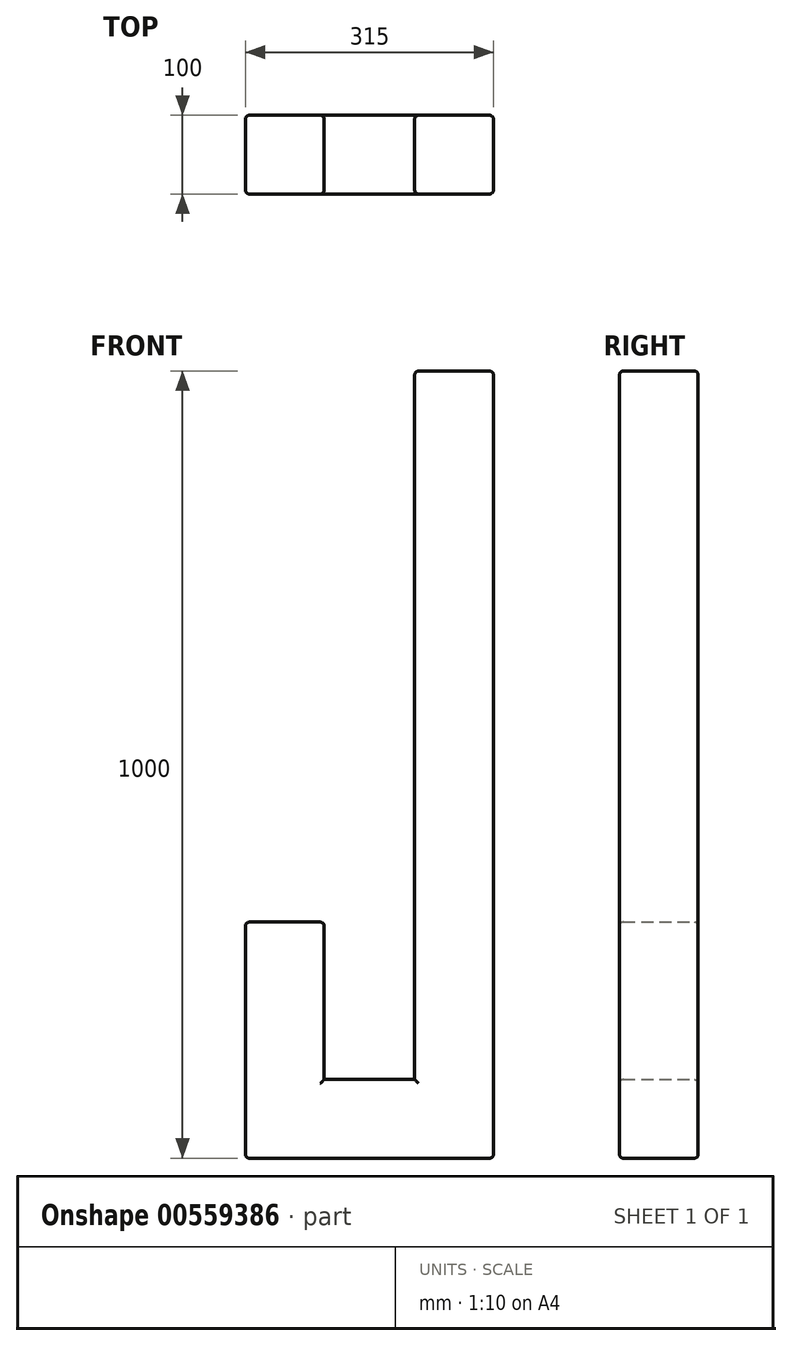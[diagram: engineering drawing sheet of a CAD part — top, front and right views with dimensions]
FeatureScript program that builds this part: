
annotation { "Feature Type Name" : "Feature", "Feature Type Description" : "" }
export const myFeature = defineFeature(function(context is Context, id is Id, definition is map)
    precondition{}
    {
        {
            var Q0;
            Q0=qCreatedBy(makeId("Front.planeOp"),FACE);
            var sketch = newSketch(context, id + "F0", { "sketchPlane" : qUnion([Q0])});
            skLineSegment(sketch, "E0", {"start": v(0, 0) * mm, "end": v(-100, 0) * mm});
            skLineSegment(sketch, "E1", {"start": v(-100, 0) * mm, "end": v(-100, -300) * mm});
            skLineSegment(sketch, "E2", {"start": v(-100, -300) * mm, "end": v(215, -300) * mm});
            skLineSegment(sketch, "E3", {"start": v(215, -300) * mm, "end": v(215, 700) * mm});
            skLineSegment(sketch, "E4", {"start": v(215, 700) * mm, "end": v(115, 700) * mm});
            skLineSegment(sketch, "E5", {"start": v(115, 700) * mm, "end": v(115, -200) * mm});
            skLineSegment(sketch, "E6", {"start": v(115, -200) * mm, "end": v(0, -200) * mm});
            skLineSegment(sketch, "E7", {"start": v(0, 0) * mm, "end": v(0, -200) * mm});
            skSolve(sketch);
        }
        {
            var Q0;
            Q0=makeQuery(id+"F0.imprint","IMPRINT",FACE,{"disambiguationData":[TD([[makeQuery(id+"F0.imprint","IMPRINT",EDGE,{"derivedFrom":sQuery(id+"F0.wireOp",EDGE,"E0")}),1.0]])]});
            extrude(context, id + "F1", {"entities" : qUnion([Q0]), "depth" : 100 * mm, "offsetDistance" : 25 * mm});
        }
        {
            var Q0;
            Q0=makeQuery(id+"F1.opExtrude","CAP_EDGE",EDGE,{"disambiguationData":[OSD([sQuery(id+"F0.wireOp",EDGE,"E1")])],"isStart":false});
            var Q1;
            Q1=makeQuery(id+"F1.opExtrude","CAP_EDGE",EDGE,{"disambiguationData":[OSD([sQuery(id+"F0.wireOp",EDGE,"E5")])],"isStart":false});
            var Q2;
            Q2=makeQuery(id+"F1.opExtrude","CAP_EDGE",EDGE,{"disambiguationData":[OSD([sQuery(id+"F0.wireOp",EDGE,"E6")])],"isStart":false});
            var Q3;
            Q3=makeQuery(id+"F1.opExtrude","CAP_EDGE",EDGE,{"disambiguationData":[OSD([sQuery(id+"F0.wireOp",EDGE,"E7")])],"isStart":false});
            var Q4;
            Q4=makeQuery(id+"F1.opExtrude","CAP_EDGE",EDGE,{"disambiguationData":[OSD([sQuery(id+"F0.wireOp",EDGE,"E0")])],"isStart":false});
            var Q5;
            Q5=makeQuery(id+"F1.opExtrude","SWEPT_EDGE",EDGE,{"disambiguationData":[OSD([sQuery(id+"F0.wireOp",EDGE,"E0"),sQuery(id+"F0.wireOp",EDGE,"E1")])]});
            var Q6;
            Q6=makeQuery(id+"F1.opExtrude","CAP_EDGE",EDGE,{"disambiguationData":[OSD([sQuery(id+"F0.wireOp",EDGE,"E1")])],"isStart":true});
            var Q7;
            Q7=makeQuery(id+"F1.opExtrude","SWEPT_EDGE",EDGE,{"disambiguationData":[OSD([sQuery(id+"F0.wireOp",EDGE,"E1"),sQuery(id+"F0.wireOp",EDGE,"E2")])]});
            var Q8;
            Q8=makeQuery(id+"F1.opExtrude","CAP_EDGE",EDGE,{"disambiguationData":[OSD([sQuery(id+"F0.wireOp",EDGE,"E2")])],"isStart":false});
            var Q9;
            Q9=makeQuery(id+"F1.opExtrude","CAP_EDGE",EDGE,{"disambiguationData":[OSD([sQuery(id+"F0.wireOp",EDGE,"E2")])],"isStart":true});
            var Q10;
            Q10=makeQuery(id+"F1.opExtrude","CAP_EDGE",EDGE,{"disambiguationData":[OSD([sQuery(id+"F0.wireOp",EDGE,"E6")])],"isStart":true});
            var Q11;
            Q11=makeQuery(id+"F1.opExtrude","CAP_EDGE",EDGE,{"disambiguationData":[OSD([sQuery(id+"F0.wireOp",EDGE,"E7")])],"isStart":true});
            var Q12;
            Q12=makeQuery(id+"F1.opExtrude","CAP_EDGE",EDGE,{"disambiguationData":[OSD([sQuery(id+"F0.wireOp",EDGE,"E0")])],"isStart":true});
            var Q13;
            Q13=makeQuery(id+"F1.opExtrude","SWEPT_EDGE",EDGE,{"disambiguationData":[OSD([sQuery(id+"F0.wireOp",EDGE,"E0"),sQuery(id+"F0.wireOp",EDGE,"E7")])]});
            var Q14;
            Q14=makeQuery(id+"F1.opExtrude","CAP_EDGE",EDGE,{"disambiguationData":[OSD([sQuery(id+"F0.wireOp",EDGE,"E5")])],"isStart":true});
            var Q15;
            Q15=makeQuery(id+"F1.opExtrude","SWEPT_EDGE",EDGE,{"disambiguationData":[OSD([sQuery(id+"F0.wireOp",EDGE,"E2"),sQuery(id+"F0.wireOp",EDGE,"E3")])]});
            var Q16;
            Q16=makeQuery(id+"F1.opExtrude","SWEPT_EDGE",EDGE,{"disambiguationData":[OSD([sQuery(id+"F0.wireOp",EDGE,"E3"),sQuery(id+"F0.wireOp",EDGE,"E4")])]});
            var Q17;
            Q17=makeQuery(id+"F1.opExtrude","CAP_EDGE",EDGE,{"disambiguationData":[OSD([sQuery(id+"F0.wireOp",EDGE,"E4")])],"isStart":true});
            var Q18;
            Q18=makeQuery(id+"F1.opExtrude","CAP_EDGE",EDGE,{"disambiguationData":[OSD([sQuery(id+"F0.wireOp",EDGE,"E4")])],"isStart":false});
            var Q19;
            Q19=makeQuery(id+"F1.opExtrude","SWEPT_EDGE",EDGE,{"disambiguationData":[OSD([sQuery(id+"F0.wireOp",EDGE,"E4"),sQuery(id+"F0.wireOp",EDGE,"E5")])]});
            var Q20;
            Q20=makeQuery(id+"F1.opExtrude","CAP_EDGE",EDGE,{"disambiguationData":[OSD([sQuery(id+"F0.wireOp",EDGE,"E3")])],"isStart":true});
            var Q21;
            Q21=makeQuery(id+"F1.opExtrude","CAP_EDGE",EDGE,{"disambiguationData":[OSD([sQuery(id+"F0.wireOp",EDGE,"E3")])],"isStart":false});
            fillet(context, id + "F2", {"entities" : qUnion([Q0, Q1, Q2, Q3, Q4, Q5, Q6, Q7, Q8, Q9, Q10, Q11, Q12, Q13, Q14, Q15, Q16, Q17, Q18, Q19, Q20, Q21]), "radius" : 5 * mm, "tangentPropagation" : true, "allowEdgeOverflow" : false});
        }
    });
